# Revit family: Indoor_Table Lamp_Santa&Cole_Gira
name_source: partatom
category: Luminarias
revit_build: Autodesk Revit 2018 (Build: 20190510_1515(x64)
units: mm (PartAtom-declared; Revit-internal decimal feet)

## family parameters
Compartido = No
Corte con vacíos al cargar = No
Cota de conector redondo = Diámetro de uso
Número OmniClass = 23.80.70.00
Origen de luz = Sí
Punto de cálculo de habitación = No
Se basa en plano de trabajo = No
Siempre vertical = Sí
Tipo de pieza = Normal
Título OmniClass = Lighting

## types (3) — shared parameters
Assembly instructions - CE = https://www.santacole.com
Assembly instructions - UL = https://www.santacole.com
Cambio de temperatura de color de luz atenuada = <Ninguno>
Carga aparente = 10 VA
Code = GIR21/GIR22/GIR23
Energy Label = https://www.santacole.com
Fabricante = Santa & Cole
Filtro de color = 16777215
Load = 10 W
Manufacturer website = http://www.santacole.com
Modelo = Gira
Tamaño de símbolo de origen de luz = 610 mm
Technical Information = https://www.santacole.com
URL = https://www.santacole.com

## per-type parameters (varying)
| type | Lampshade Material |
| Brass Shade | Santa & Cole - Semi Brass |
| Black anodized aluminium | Santa & Cole - Black Anodized Aluminium |
| Natural anodized aluminium | Santa & Cole - Natural Anodized Aluminium |

## geometry (parser evidence)
native form markers: Sweep x3
no freeform markers — native parametric forms only
